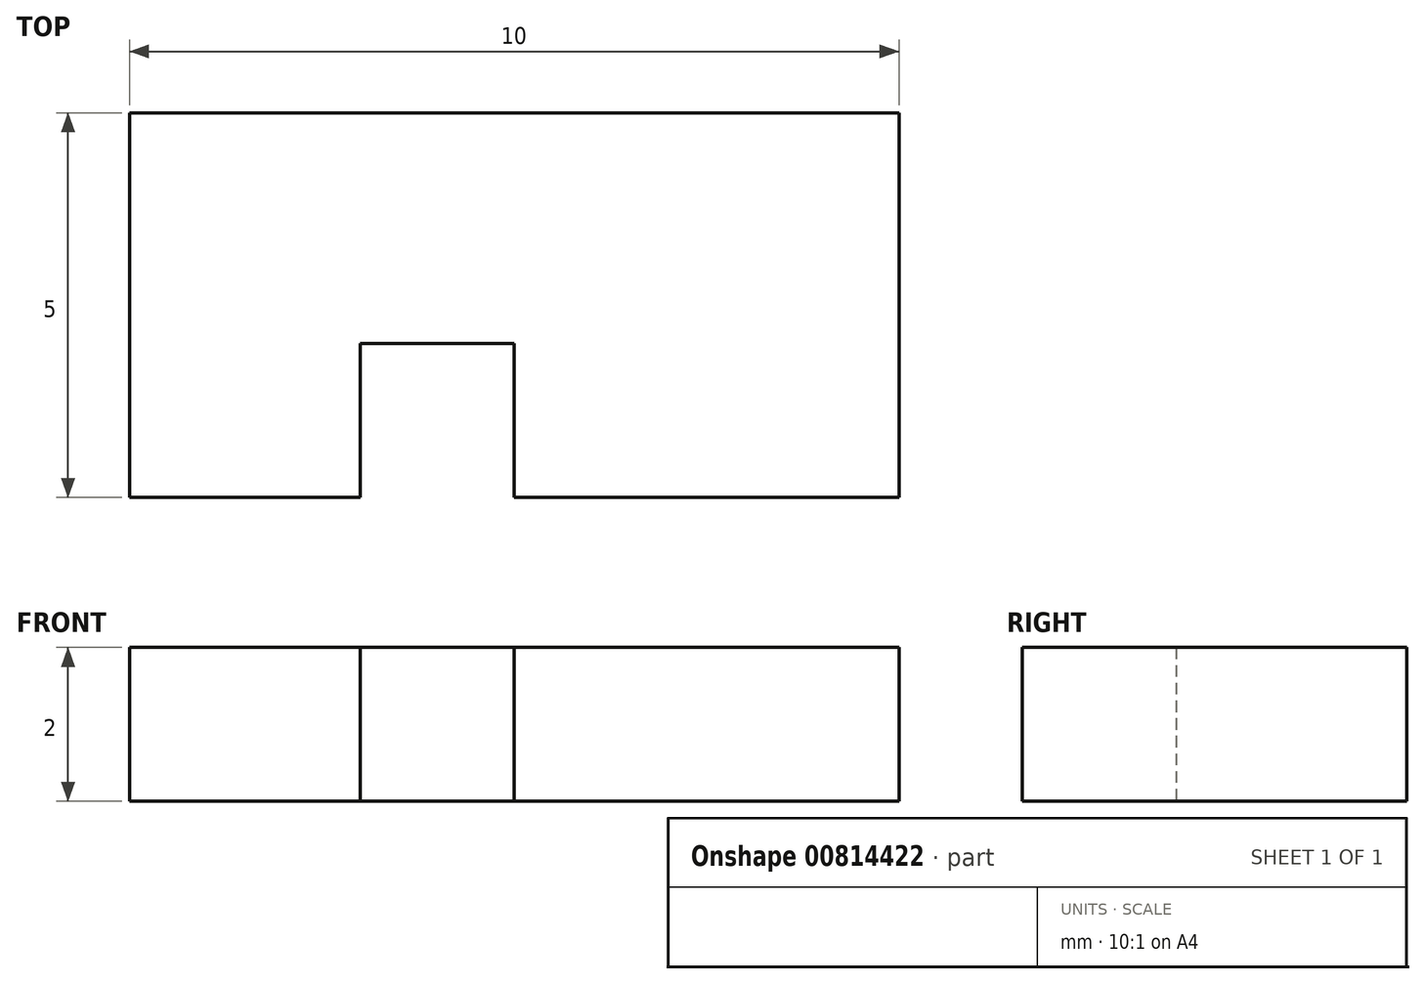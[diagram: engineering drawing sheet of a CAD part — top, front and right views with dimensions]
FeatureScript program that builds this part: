
annotation { "Feature Type Name" : "Feature", "Feature Type Description" : "" }
export const myFeature = defineFeature(function(context is Context, id is Id, definition is map)
    precondition{}
    {
        {
            var Q0;
            Q0=qCreatedBy(makeId("Top.planeOp"),FACE);
            var sketch = newSketch(context, id + "F0", { "sketchPlane" : qUnion([Q0])});
            skLineSegment(sketch, "E0.bottom", {"start": v(0, 0) * mm, "end": v(10, 0) * mm});
            skLineSegment(sketch, "E0.top", {"start": v(0, -5) * mm, "end": v(10, -5) * mm});
            skLineSegment(sketch, "E0.left", {"start": v(0, 0) * mm, "end": v(0, -5) * mm});
            skLineSegment(sketch, "E0.right", {"start": v(10, 0) * mm, "end": v(10, -5) * mm});
            skLineSegment(sketch, "E1.bottom", {"start": v(3, -5) * mm, "end": v(5, -5) * mm});
            skLineSegment(sketch, "E1.top", {"start": v(3, -3) * mm, "end": v(5, -3) * mm});
            skLineSegment(sketch, "E1.left", {"start": v(3, -5) * mm, "end": v(3, -3) * mm});
            skLineSegment(sketch, "E1.right", {"start": v(5, -5) * mm, "end": v(5, -3) * mm});
            skSolve(sketch);
        }
        {
            var Q0;
            Q0=makeQuery(id+"F0.imprint","IMPRINT",FACE,{"disambiguationData":[TD([[makeQuery(id+"F0.imprint","IMPRINT",EDGE,{"derivedFrom":sQuery(id+"F0.wireOp",EDGE,"E0.bottom")}),-1.0]])]});
            extrude(context, id + "F1", {"entities" : qUnion([Q0]), "depth" : 2 * mm, "offsetDistance" : 25 * mm});
        }
    });
